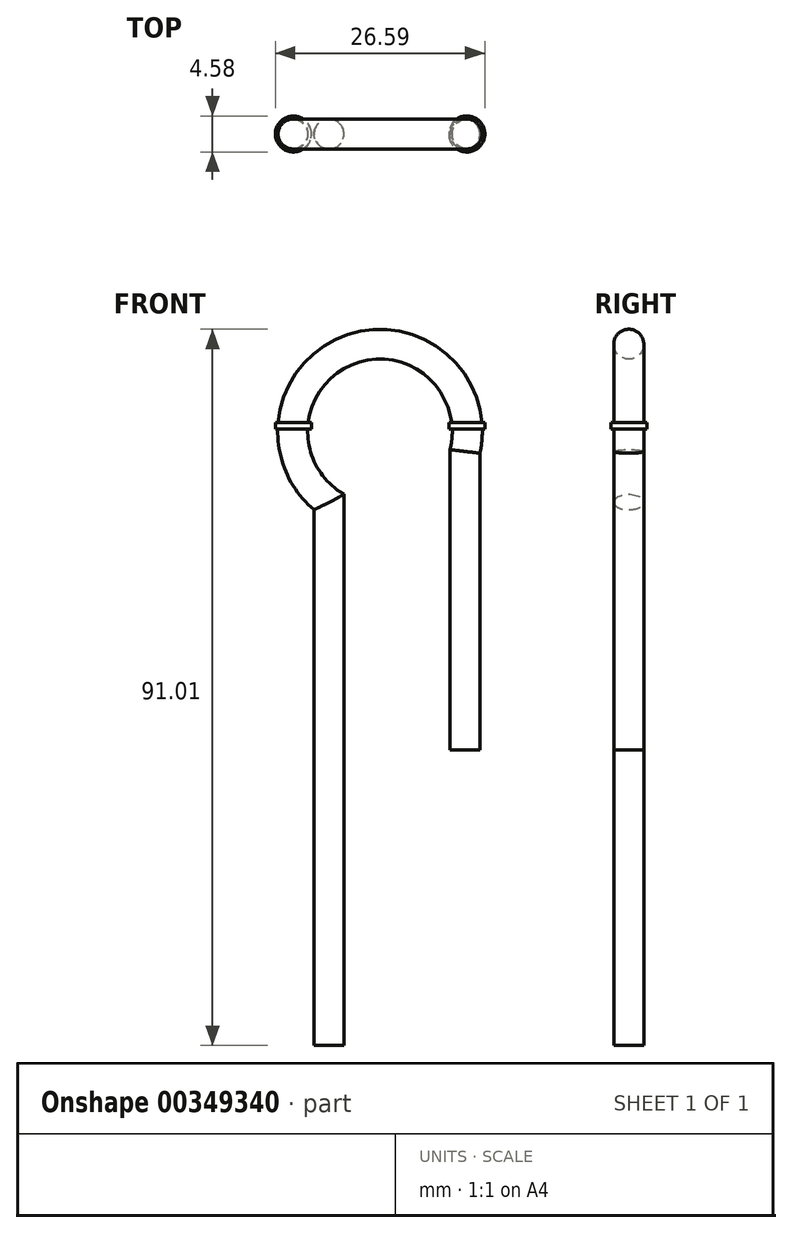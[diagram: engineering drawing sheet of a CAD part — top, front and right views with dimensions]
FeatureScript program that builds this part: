
annotation { "Feature Type Name" : "Feature", "Feature Type Description" : "" }
export const myFeature = defineFeature(function(context is Context, id is Id, definition is map)
    precondition{}
    {
        {
            var Q0;
            Q0=qCreatedBy(makeId("Front.planeOp"),FACE);
            var sketch = newSketch(context, id + "F0", { "sketchPlane" : qUnion([Q0])});
            skArc(sketch, "E0", {"start": v(14.14, -2.67) * mm, "mid": v(1.29, 8.5) * mm, "end": v(0, -8.48) * mm});
            skLineSegment(sketch, "E1", {"start": v(14.14, -2.67) * mm, "end": v(14.14, -40.77) * mm});
            skLineSegment(sketch, "E2", {"start": v(0, -8.48) * mm, "end": v(0, -78.33) * mm});
            skSolve(sketch);
        }
        {
            var Q0;
            Q0=qCreatedBy(makeId("Top.planeOp"),FACE);
            cPlane(context, id + "F1", {"entities" : qUnion([Q0]), "cplaneType" : CPlaneType.OFFSET, "offset" : 40.64 * mm, "oppositeDirection" : true, "width" : 152.4 * mm, "height" : 152.4 * mm});
        }
        {
            var Q0;
            Q0=qCreatedBy(id+"F1.planeOp",FACE);
            var sketch = newSketch(context, id + "F2", { "sketchPlane" : qUnion([Q0])});
            skCircle(sketch, "E3", {"center": v(15.7, 0) * mm, "radius": 1.9 * mm});
            skSolve(sketch);
        }
        {
            var Q0;
            Q0=makeQuery(id+"F2.imprint","IMPRINT",FACE,{"disambiguationData":[TD([[makeQuery(id+"F2.imprint","IMPRINT",EDGE,{"derivedFrom":sQuery(id+"F2.wireOp",EDGE,"E3")}),1.0]])]});
            var Q1;
            Q1=sQuery(id+"F0.wireOp",EDGE,"E1");
            var Q2;
            Q2=sQuery(id+"F0.wireOp",EDGE,"E0");
            var Q3;
            Q3=sQuery(id+"F0.wireOp",EDGE,"E2");
            sweep(context, id + "F3", {"profiles" : qUnion([Q0]), "path" : qUnion([Q1, Q2, Q3])});
        }
        {
            var Q0;
            Q0=qCreatedBy(makeId("Top.planeOp"),FACE);
            var sketch = newSketch(context, id + "F4", { "sketchPlane" : qUnion([Q0])});
            skCircle(sketch, "E4", {"center": v(15.94, 0) * mm, "radius": 2.29 * mm});
            skCircle(sketch, "E5.1.0", {"center": v(-6.08, 0) * mm, "radius": 2.29 * mm});
            skPoint(sketch, "E5.center", {"position": v(4.93, 0) * mm});
            skLineSegment(sketch, "E5.anchor1", {"start": v(4.93, 0) * mm, "end": v(15.94, 0) * mm, "construction": true});
            skLineSegment(sketch, "E5.anchor2", {"start": v(4.93, 0) * mm, "end": v(-6.08, 0) * mm, "construction": true});
            skSolve(sketch);
        }
        {
            var Q0;
            Q0=makeQuery(id+"F4.imprint","IMPRINT",FACE,{"disambiguationData":[TD([[makeQuery(id+"F4.imprint","IMPRINT",EDGE,{"derivedFrom":sQuery(id+"F4.wireOp",EDGE,"E4")}),1.0]])]});
            var Q1;
            Q1=makeQuery(id+"F4.imprint","IMPRINT",FACE,{"disambiguationData":[TD([[makeQuery(id+"F4.imprint","IMPRINT",EDGE,{"derivedFrom":sQuery(id+"F4.wireOp",EDGE,"E5.1.0")}),1.0]])]});
            var Q2;
            Q2=sQuery(id+"F4.wireOp",EDGE,"E4");
            extrude(context, id + "F5", {"entities" : qUnion([Q0, Q1]), "operationType" : NewBodyOperationType.ADD, "surfaceEntities" : qUnion([Q2]), "depth" : 0.8 * mm});
        }
    });
